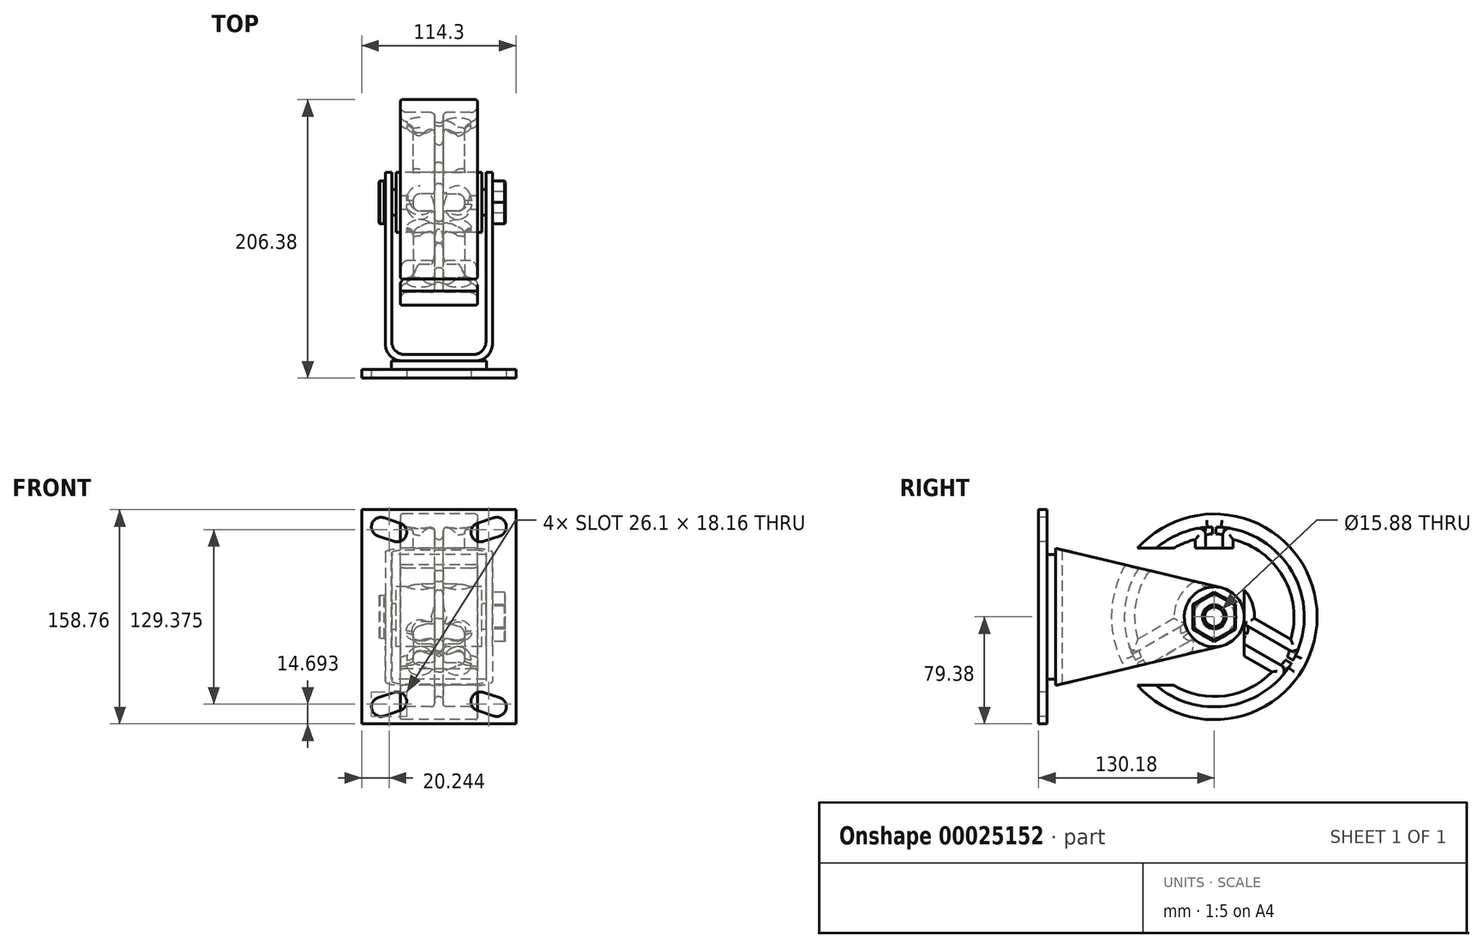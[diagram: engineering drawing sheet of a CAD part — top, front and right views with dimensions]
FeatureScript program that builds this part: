
annotation { "Feature Type Name" : "Feature", "Feature Type Description" : "" }
export const myFeature = defineFeature(function(context is Context, id is Id, definition is map)
    precondition{}
    {
        {
            var Q0;
            Q0=qCreatedBy(makeId("Right.planeOp"),FACE);
            var sketch = newSketch(context, id + "F0", { "sketchPlane" : qUnion([Q0])});
            skCircle(sketch, "E0", {"center": v(0, 0) * mm, "radius": 76.2 * mm});
            skCircle(sketch, "E1", {"center": v(0, 0) * mm, "radius": 9.53 * mm});
            skCircle(sketch, "E2.0", {"center": v(0, 0) * mm, "radius": 66.67 * mm});
            skCircle(sketch, "E3.0", {"center": v(0, 0) * mm, "radius": 22.23 * mm});
            skSolve(sketch);
        }
        {
            var Q0;
            Q0=qSketchRegion(id+"F0",true);
            extrude(context, id + "F1", {"entities" : qUnion([Q0]), "endBound" : BoundingType.SYMMETRIC, "depth" : 57.15 * mm});
        }
        {
            var Q0;
            Q0=makeQuery(id+"F0.imprint","IMPRINT",FACE,{"disambiguationData":[TD([[makeQuery(id+"F0.imprint","IMPRINT",EDGE,{"derivedFrom":sQuery(id+"F0.wireOp",EDGE,"E2.0")}),1.0]])]});
            var Q1;
            Q1=makeQuery(id+"F0.imprint","IMPRINT",FACE,{"disambiguationData":[TD([[makeQuery(id+"F0.imprint","IMPRINT",EDGE,{"derivedFrom":sQuery(id+"F0.wireOp",EDGE,"E1")}),-1.0]])]});
            extrude(context, id + "F2", {"entities" : qUnion([Q0, Q1]), "operationType" : NewBodyOperationType.ADD, "endBound" : BoundingType.SYMMETRIC, "depth" : 6.35 * mm});
        }
        {
            var Q0;
            Q0=qCreatedBy(makeId("Right.planeOp"),FACE);
            var sketch = newSketch(context, id + "F3", { "sketchPlane" : qUnion([Q0])});
            skCircle(sketch, "E4.0", {"center": v(0, 0) * mm, "radius": 22.23 * mm});
            skCircle(sketch, "E5.0", {"center": v(0, 0) * mm, "radius": 9.53 * mm});
            skSolve(sketch);
        }
        {
            var Q0;
            Q0=qSketchRegion(id+"F3",true);
            extrude(context, id + "F4", {"entities" : qUnion([Q0]), "operationType" : NewBodyOperationType.ADD, "endBound" : BoundingType.SYMMETRIC, "depth" : 63.5 * mm});
        }
        {
            var Q0;
            Q0=qCreatedBy(makeId("Right.planeOp"),FACE);
            var sketch = newSketch(context, id + "F5", { "sketchPlane" : qUnion([Q0])});
            skArc(sketch, "E6.0", {"start": v(-60.65, -27.69) * mm, "mid": v(-57.74, -33.34) * mm, "end": v(-54.3, -38.69) * mm});
            skArc(sketch, "E7.0", {"start": v(15.27, -16.15) * mm, "mid": v(19.25, -11.11) * mm, "end": v(21.62, -5.15) * mm});
            skLineSegment(sketch, "E8", {"start": v(0, 0) * mm, "end": v(0, 89.96) * mm, "construction": true});
            skLineSegment(sketch, "E9.0", {"start": v(-6.35, 21.3) * mm, "end": v(-6.35, 66.37) * mm});
            skLineSegment(sketch, "E10.0.MirrorCS", {"start": v(6.35, 21.3) * mm, "end": v(6.35, 66.37) * mm});
            skLineSegment(sketch, "E11.1.0", {"start": v(-15.27, -16.15) * mm, "end": v(-54.3, -38.69) * mm});
            skLineSegment(sketch, "E11.1.1", {"start": v(-21.62, -5.15) * mm, "end": v(-60.65, -27.69) * mm});
            skLineSegment(sketch, "E11.2.0", {"start": v(21.62, -5.15) * mm, "end": v(60.65, -27.69) * mm});
            skLineSegment(sketch, "E11.2.1", {"start": v(15.27, -16.15) * mm, "end": v(54.3, -38.69) * mm});
            skArc(sketch, "E12.trimOffspring", {"start": v(6.35, 66.37) * mm, "mid": v(0, 66.67) * mm, "end": v(-6.35, 66.37) * mm});
            skArc(sketch, "E13.trimOffspring", {"start": v(54.3, -38.69) * mm, "mid": v(57.74, -33.34) * mm, "end": v(60.65, -27.69) * mm});
            skArc(sketch, "E14.trimOffspring", {"start": v(-21.62, -5.15) * mm, "mid": v(-19.25, -11.11) * mm, "end": v(-15.27, -16.15) * mm});
            skArc(sketch, "E15.trimOffspring", {"start": v(6.35, 21.3) * mm, "mid": v(0, 22.22) * mm, "end": v(-6.35, 21.3) * mm});
            skSolve(sketch);
        }
        {
            var Q0;
            Q0=qSketchRegion(id+"F5",true);
            extrude(context, id + "F6", {"entities" : qUnion([Q0]), "operationType" : NewBodyOperationType.ADD, "endBound" : BoundingType.SYMMETRIC, "depth" : 38.1 * mm});
        }
        {
            var Q0;
            {var subQ0=sQuery(id+"F0.wireOp",EDGE,"E2.0");Q0=makeQuery(id+"F6.boolean.opBoolean","SPLIT",FACE,{"disambiguationData":[TD([makeQuery(id+"F6.opExtrude","SWEPT_FACE",FACE,{"disambiguationData":[OSD([sQuery(id+"F5.wireOp",EDGE,"E11.1.0")])]})])],"derivedFrom":makeQuery(id+"F2.opExtrude","CAP_FACE",FACE,{"disambiguationData":[OSD([sQuery(id+"F0.wireOp",EDGE,"E1"),subQ0])],"isStart":false})});}
            var sketch = newSketch(context, id + "F7", { "sketchPlane" : qUnion([Q0])});
            skArc(sketch, "E16.0", {"start": v(-15.86, -25.29) * mm, "mid": v(0, -29.85) * mm, "end": v(15.86, -25.29) * mm});
            skLineSegment(sketch, "E17.0", {"start": v(-15.86, -25.29) * mm, "end": v(-42.7, -40.79) * mm});
            skArc(sketch, "E18.0", {"start": v(-42.7, -40.79) * mm, "mid": v(0, -59.05) * mm, "end": v(42.7, -40.79) * mm});
            skLineSegment(sketch, "E19.0", {"start": v(15.86, -25.29) * mm, "end": v(42.7, -40.79) * mm});
            skArc(sketch, "E20.1.0", {"start": v(29.83, -1.09) * mm, "mid": v(25.85, 14.92) * mm, "end": v(13.97, 26.37) * mm});
            skLineSegment(sketch, "E20.1.1", {"start": v(13.97, 26.37) * mm, "end": v(13.97, 57.38) * mm});
            skArc(sketch, "E20.1.2", {"start": v(56.68, -16.6) * mm, "mid": v(51.14, 29.53) * mm, "end": v(13.97, 57.38) * mm});
            skLineSegment(sketch, "E20.1.3", {"start": v(29.83, -1.09) * mm, "end": v(56.68, -16.6) * mm});
            skArc(sketch, "E20.2.0", {"start": v(-13.97, 26.37) * mm, "mid": v(-25.85, 14.92) * mm, "end": v(-29.83, -1.09) * mm});
            skLineSegment(sketch, "E20.2.1", {"start": v(-29.83, -1.09) * mm, "end": v(-56.68, -16.6) * mm});
            skArc(sketch, "E20.2.2", {"start": v(-13.97, 57.38) * mm, "mid": v(-51.14, 29.53) * mm, "end": v(-56.68, -16.6) * mm});
            skLineSegment(sketch, "E20.2.3", {"start": v(-13.97, 26.37) * mm, "end": v(-13.97, 57.38) * mm});
            skSolve(sketch);
        }
        {
            var Q0;
            Q0=qSketchRegion(id+"F7",true);
            extrude(context, id + "F8", {"entities" : qUnion([Q0]), "operationType" : NewBodyOperationType.REMOVE, "endBound" : BoundingType.THROUGH_ALL, "oppositeDirection" : true, "depth" : 25.4 * mm});
        }
        {
            var Q0;
            {var subQ0=sQuery(id+"F0.wireOp",EDGE,"E2.0");Q0=makeQuery(id+"F6.boolean.opBoolean","SPLIT",FACE,{"disambiguationData":[TD([makeQuery(id+"F6.opExtrude","SWEPT_FACE",FACE,{"disambiguationData":[OSD([sQuery(id+"F5.wireOp",EDGE,"E10.0.MirrorCS")])]})])],"derivedFrom":makeQuery(id+"F2.opExtrude","CAP_FACE",FACE,{"disambiguationData":[OSD([sQuery(id+"F0.wireOp",EDGE,"E1"),subQ0])],"isStart":false})});}
            var Q1;
            {var subQ0=sQuery(id+"F0.wireOp",EDGE,"E2.0");Q1=makeQuery(id+"F6.boolean.opBoolean","SPLIT",FACE,{"disambiguationData":[TD([makeQuery(id+"F6.opExtrude","SWEPT_FACE",FACE,{"disambiguationData":[OSD([sQuery(id+"F5.wireOp",EDGE,"E9.0")])]})])],"derivedFrom":makeQuery(id+"F2.opExtrude","CAP_FACE",FACE,{"disambiguationData":[OSD([sQuery(id+"F0.wireOp",EDGE,"E1"),subQ0])],"isStart":false})});}
            var Q2;
            {var subQ0=sQuery(id+"F0.wireOp",EDGE,"E2.0");Q2=makeQuery(id+"F6.boolean.opBoolean","SPLIT",FACE,{"disambiguationData":[TD([makeQuery(id+"F6.opExtrude","SWEPT_FACE",FACE,{"disambiguationData":[OSD([sQuery(id+"F5.wireOp",EDGE,"E11.1.0")])]})])],"derivedFrom":makeQuery(id+"F2.opExtrude","CAP_FACE",FACE,{"disambiguationData":[OSD([sQuery(id+"F0.wireOp",EDGE,"E1"),subQ0])],"isStart":false})});}
            var Q3;
            {var subQ0=sQuery(id+"F0.wireOp",EDGE,"E2.0");Q3=makeQuery(id+"F6.boolean.opBoolean","SPLIT",FACE,{"disambiguationData":[TD([makeQuery(id+"F6.opExtrude","SWEPT_FACE",FACE,{"disambiguationData":[OSD([sQuery(id+"F5.wireOp",EDGE,"E11.1.0")])]})])],"derivedFrom":makeQuery(id+"F2.opExtrude","CAP_FACE",FACE,{"disambiguationData":[OSD([sQuery(id+"F0.wireOp",EDGE,"E1"),subQ0])],"isStart":true})});}
            var Q4;
            {var subQ0=sQuery(id+"F0.wireOp",EDGE,"E2.0");Q4=makeQuery(id+"F6.boolean.opBoolean","SPLIT",FACE,{"disambiguationData":[TD([makeQuery(id+"F6.opExtrude","SWEPT_FACE",FACE,{"disambiguationData":[OSD([sQuery(id+"F5.wireOp",EDGE,"E10.0.MirrorCS")])]})])],"derivedFrom":makeQuery(id+"F2.opExtrude","CAP_FACE",FACE,{"disambiguationData":[OSD([sQuery(id+"F0.wireOp",EDGE,"E1"),subQ0])],"isStart":true})});}
            var Q5;
            {var subQ0=sQuery(id+"F0.wireOp",EDGE,"E2.0");Q5=makeQuery(id+"F6.boolean.opBoolean","SPLIT",FACE,{"disambiguationData":[TD([makeQuery(id+"F6.opExtrude","SWEPT_FACE",FACE,{"disambiguationData":[OSD([sQuery(id+"F5.wireOp",EDGE,"E9.0")])]})])],"derivedFrom":makeQuery(id+"F2.opExtrude","CAP_FACE",FACE,{"disambiguationData":[OSD([sQuery(id+"F0.wireOp",EDGE,"E1"),subQ0])],"isStart":true})});}
            fillet(context, id + "F9", {"entities" : qUnion([Q0, Q1, Q2, Q3, Q4, Q5]), "radius" : 2.54 * mm, "tangentPropagation" : true, "allowEdgeOverflow" : false});
        }
        {
            var Q0;
            Q0=makeQuery(id+"F6.opExtrude","CAP_FACE",FACE,{"disambiguationData":[OSD([sQuery(id+"F5.wireOp",EDGE,"E9.0"),sQuery(id+"F5.wireOp",EDGE,"E10.0.MirrorCS"),sQuery(id+"F5.wireOp",EDGE,"E12.trimOffspring"),sQuery(id+"F5.wireOp",EDGE,"E15.trimOffspring")])],"isStart":true});
            var Q1;
            {var subQ0=sQuery(id+"F5.wireOp",EDGE,"E10.0.MirrorCS");var subQ1=sQuery(id+"F0.wireOp",EDGE,"E2.0");Q1=makeQuery(id+"F6.boolean.opBoolean","SPLIT",FACE,{"disambiguationData":[TD([makeQuery(id+"F2.opExtrude","CAP_FACE",FACE,{"disambiguationData":[OSD([sQuery(id+"F0.wireOp",EDGE,"E1"),subQ1])],"isStart":true})])],"derivedFrom":makeQuery(id+"F6.opExtrude","SWEPT_FACE",FACE,{"disambiguationData":[OSD([subQ0])]})});}
            var Q2;
            {var subQ0=sQuery(id+"F5.wireOp",EDGE,"E11.2.0");var subQ1=sQuery(id+"F0.wireOp",EDGE,"E2.0");Q2=makeQuery(id+"F6.boolean.opBoolean","SPLIT",FACE,{"disambiguationData":[TD([makeQuery(id+"F2.opExtrude","CAP_FACE",FACE,{"disambiguationData":[OSD([sQuery(id+"F0.wireOp",EDGE,"E1"),subQ1])],"isStart":true})])],"derivedFrom":makeQuery(id+"F6.opExtrude","SWEPT_FACE",FACE,{"disambiguationData":[OSD([subQ0])]})});}
            var Q3;
            Q3=makeQuery(id+"F6.opExtrude","CAP_FACE",FACE,{"disambiguationData":[OSD([sQuery(id+"F5.wireOp",EDGE,"E7.0"),sQuery(id+"F5.wireOp",EDGE,"E11.2.0"),sQuery(id+"F5.wireOp",EDGE,"E11.2.1"),sQuery(id+"F5.wireOp",EDGE,"E13.trimOffspring")])],"isStart":true});
            var Q4;
            Q4=makeQuery(id+"F6.opExtrude","CAP_FACE",FACE,{"disambiguationData":[OSD([sQuery(id+"F5.wireOp",EDGE,"E6.0"),sQuery(id+"F5.wireOp",EDGE,"E11.1.0"),sQuery(id+"F5.wireOp",EDGE,"E11.1.1"),sQuery(id+"F5.wireOp",EDGE,"E14.trimOffspring")])],"isStart":true});
            var Q5;
            Q5=makeQuery(id+"F6.opExtrude","CAP_FACE",FACE,{"disambiguationData":[OSD([sQuery(id+"F5.wireOp",EDGE,"E9.0"),sQuery(id+"F5.wireOp",EDGE,"E10.0.MirrorCS"),sQuery(id+"F5.wireOp",EDGE,"E12.trimOffspring"),sQuery(id+"F5.wireOp",EDGE,"E15.trimOffspring")])],"isStart":false});
            var Q6;
            Q6=makeQuery(id+"F6.opExtrude","CAP_FACE",FACE,{"disambiguationData":[OSD([sQuery(id+"F5.wireOp",EDGE,"E6.0"),sQuery(id+"F5.wireOp",EDGE,"E11.1.0"),sQuery(id+"F5.wireOp",EDGE,"E11.1.1"),sQuery(id+"F5.wireOp",EDGE,"E14.trimOffspring")])],"isStart":false});
            var Q7;
            Q7=makeQuery(id+"F6.opExtrude","CAP_FACE",FACE,{"disambiguationData":[OSD([sQuery(id+"F5.wireOp",EDGE,"E7.0"),sQuery(id+"F5.wireOp",EDGE,"E11.2.0"),sQuery(id+"F5.wireOp",EDGE,"E11.2.1"),sQuery(id+"F5.wireOp",EDGE,"E13.trimOffspring")])],"isStart":false});
            fillet(context, id + "F10", {"entities" : qUnion([Q0, Q1, Q2, Q3, Q4, Q5, Q6, Q7]), "radius" : 5.08 * mm, "tangentPropagation" : true, "allowEdgeOverflow" : false});
        }
        {
            var Q0;
            Q0=makeQuery(id+"F1.opExtrude","CAP_EDGE",EDGE,{"disambiguationData":[OSD([sQuery(id+"F0.wireOp",EDGE,"E2.0")])],"isStart":false});
            var Q1;
            Q1=makeQuery(id+"F1.opExtrude","CAP_EDGE",EDGE,{"disambiguationData":[OSD([sQuery(id+"F0.wireOp",EDGE,"E2.0")])],"isStart":true});
            fillet(context, id + "F11", {"entities" : qUnion([Q0, Q1]), "radius" : 5.08 * mm, "tangentPropagation" : true, "allowEdgeOverflow" : false});
        }
        {
            var Q0;
            Q0=makeQuery(id+"F1.opExtrude","SWEPT_FACE",FACE,{"disambiguationData":[OSD([sQuery(id+"F0.wireOp",EDGE,"E0")])]});
            fillet(context, id + "F12", {"entities" : qUnion([Q0]), "radius" : 1.52 * mm, "tangentPropagation" : true, "allowEdgeOverflow" : false});
        }
        {
            var Q0;
            Q0=qCreatedBy(makeId("Front.planeOp"),FACE);
            cPlane(context, id + "F13", {"entities" : qUnion([Q0]), "cplaneType" : CPlaneType.OFFSET, "offset" : 130.17 * mm, "width" : 152.4 * mm, "height" : 152.4 * mm});
        }
        {
            var Q0;
            Q0=qCreatedBy(id+"F13.planeOp",FACE);
            var sketch = newSketch(context, id + "F14", { "sketchPlane" : qUnion([Q0])});
            skLineSegment(sketch, "E21.rect.bottom", {"start": v(57.15, 79.38) * mm, "end": v(-57.15, 79.38) * mm});
            skLineSegment(sketch, "E21.rect.top", {"start": v(57.15, -79.38) * mm, "end": v(-57.15, -79.38) * mm});
            skLineSegment(sketch, "E21.rect.left", {"start": v(57.15, 79.38) * mm, "end": v(57.15, -79.38) * mm});
            skLineSegment(sketch, "E21.rect.right", {"start": v(-57.15, 79.38) * mm, "end": v(-57.15, -79.38) * mm});
            skPoint(sketch, "E21.rect.middle", {"position": v(0, 0) * mm});
            skLineSegment(sketch, "E22", {"start": v(57.15, 0) * mm, "end": v(-57.15, 0) * mm, "construction": true});
            skLineSegment(sketch, "E23", {"start": v(0, 79.38) * mm, "end": v(0, -79.38) * mm, "construction": true});
            skLineSegment(sketch, "E24.0", {"start": v(57.15, 66.68) * mm, "end": v(-57.15, 66.67) * mm, "construction": true});
            skLineSegment(sketch, "E25.0", {"start": v(57.15, 62.7) * mm, "end": v(-57.15, 62.7) * mm, "construction": true});
            skLineSegment(sketch, "E26.0", {"start": v(42.86, 76.2) * mm, "end": v(42.86, -76.2) * mm, "construction": true});
            skLineSegment(sketch, "E27.0", {"start": v(30.95, 76.2) * mm, "end": v(30.95, -76.2) * mm, "construction": true});
            skArc(sketch, "E28", {"start": v(28.7, 69.45) * mm, "mid": v(24.2, 60.45) * mm, "end": v(33.2, 55.95) * mm});
            skLineSegment(sketch, "E29", {"start": v(45.11, 59.93) * mm, "end": v(33.2, 55.95) * mm});
            skLineSegment(sketch, "E30", {"start": v(28.7, 69.45) * mm, "end": v(40.61, 73.42) * mm});
            skArc(sketch, "E31.trimOffspring", {"start": v(45.11, 59.93) * mm, "mid": v(49.6, 68.93) * mm, "end": v(40.61, 73.42) * mm});
            skArc(sketch, "E32.0.MirrorCS", {"start": v(45.11, -59.93) * mm, "mid": v(49.6, -68.93) * mm, "end": v(40.61, -73.42) * mm});
            skLineSegment(sketch, "E33.0.MirrorCS", {"start": v(28.7, -69.45) * mm, "end": v(40.61, -73.42) * mm});
            skLineSegment(sketch, "E34.0.MirrorCS", {"start": v(45.11, -59.93) * mm, "end": v(33.2, -55.95) * mm});
            skArc(sketch, "E35.0.MirrorCS", {"start": v(28.7, -69.45) * mm, "mid": v(24.2, -60.45) * mm, "end": v(33.2, -55.95) * mm});
            skLineSegment(sketch, "E36.0.MirrorCS", {"start": v(-45.11, -59.93) * mm, "end": v(-33.2, -55.95) * mm});
            skLineSegment(sketch, "E36.1.MirrorCS", {"start": v(-28.7, -69.45) * mm, "end": v(-40.61, -73.42) * mm});
            skLineSegment(sketch, "E36.2.MirrorCS", {"start": v(-42.86, 76.2) * mm, "end": v(-42.86, -76.2) * mm, "construction": true});
            skArc(sketch, "E36.3.MirrorCS", {"start": v(-28.7, 69.45) * mm, "mid": v(-24.2, 60.45) * mm, "end": v(-33.2, 55.95) * mm});
            skArc(sketch, "E36.4.MirrorCS", {"start": v(-45.11, -59.93) * mm, "mid": v(-49.6, -68.93) * mm, "end": v(-40.61, -73.42) * mm});
            skLineSegment(sketch, "E36.5.MirrorCS", {"start": v(-28.7, 69.45) * mm, "end": v(-40.61, 73.42) * mm});
            skArc(sketch, "E36.6.MirrorCS", {"start": v(-45.11, 59.93) * mm, "mid": v(-49.6, 68.93) * mm, "end": v(-40.61, 73.42) * mm});
            skLineSegment(sketch, "E36.7.MirrorCS", {"start": v(-30.95, 76.2) * mm, "end": v(-30.95, -76.2) * mm, "construction": true});
            skLineSegment(sketch, "E36.8.MirrorCS", {"start": v(-45.11, 59.93) * mm, "end": v(-33.2, 55.95) * mm});
            skArc(sketch, "E36.9.MirrorCS", {"start": v(-28.7, -69.45) * mm, "mid": v(-24.2, -60.45) * mm, "end": v(-33.2, -55.95) * mm});
            skSolve(sketch);
        }
        {
            var Q0;
            Q0=makeQuery(id+"F14.imprint","IMPRINT",FACE,{"disambiguationData":[TD([[makeQuery(id+"F14.imprint","IMPRINT",EDGE,{"derivedFrom":sQuery(id+"F14.wireOp",EDGE,"E21.rect.bottom")}),1.0]])]});
            extrude(context, id + "F15", {"entities" : qUnion([Q0]), "oppositeDirection" : true, "depth" : 6.38 * mm});
        }
        {
            var Q0;
            Q0=qCreatedBy(makeId("Top.planeOp"),FACE);
            var sketch = newSketch(context, id + "F16", { "sketchPlane" : qUnion([Q0])});
            skLineSegment(sketch, "E37.0", {"start": v(-34.92, 22.23) * mm, "end": v(-34.92, -112.67) * mm});
            skLineSegment(sketch, "E38.0", {"start": v(0, -117.45) * mm, "end": v(-39.7, -117.45) * mm});
            skLineSegment(sketch, "E39.0", {"start": v(0, -112.67) * mm, "end": v(-34.92, -112.67) * mm});
            skLineSegment(sketch, "E40.0", {"start": v(-39.7, 22.23) * mm, "end": v(-39.7, -117.45) * mm});
            skLineSegment(sketch, "E41", {"start": v(0, 0) * mm, "end": v(0, -149.02) * mm, "construction": true});
            skLineSegment(sketch, "E42", {"start": v(-39.7, 22.23) * mm, "end": v(-34.92, 22.23) * mm});
            skLineSegment(sketch, "E43.0.MirrorCS", {"start": v(0, -112.67) * mm, "end": v(34.92, -112.67) * mm});
            skLineSegment(sketch, "E44.0.MirrorCS", {"start": v(0, -117.45) * mm, "end": v(39.7, -117.45) * mm});
            skLineSegment(sketch, "E45.0.MirrorCS", {"start": v(34.92, 22.23) * mm, "end": v(34.92, -112.67) * mm});
            skLineSegment(sketch, "E46.0.MirrorCS", {"start": v(39.7, 22.23) * mm, "end": v(39.7, -117.45) * mm});
            skLineSegment(sketch, "E47.0.MirrorCS", {"start": v(39.7, 22.23) * mm, "end": v(34.92, 22.23) * mm});
            skSolve(sketch);
        }
        {
            var Q0;
            Q0=qSketchRegion(id+"F16",true);
            extrude(context, id + "F17", {"entities" : qUnion([Q0]), "endBound" : BoundingType.SYMMETRIC, "depth" : 101.6 * mm});
        }
        {
            var Q0;
            Q0=makeQuery(id+"F17.opExtrude","SWEPT_FACE",FACE,{"disambiguationData":[OSD([sQuery(id+"F16.wireOp",EDGE,"E40.0")])]});
            var sketch = newSketch(context, id + "F18", { "sketchPlane" : qUnion([Q0])});
            skArc(sketch, "E48.0", {"start": v(-5.15, -21.62) * mm, "mid": v(-22.23, 0) * mm, "end": v(-5.15, 21.62) * mm});
            skLineSegment(sketch, "E49", {"start": v(117.45, 50.8) * mm, "end": v(-5.15, 21.62) * mm});
            skLineSegment(sketch, "E50", {"start": v(117.45, -50.8) * mm, "end": v(-5.15, -21.62) * mm});
            skCircle(sketch, "E51.0", {"center": v(0, 0) * mm, "radius": 9.53 * mm});
            skLineSegment(sketch, "E52.0", {"start": v(-22.23, 50.8) * mm, "end": v(117.45, 50.8) * mm});
            skLineSegment(sketch, "E53.0", {"start": v(-22.23, 50.8) * mm, "end": v(-22.23, -50.8) * mm});
            skLineSegment(sketch, "E54.0", {"start": v(-22.23, -50.8) * mm, "end": v(117.45, -50.8) * mm});
            skSolve(sketch);
        }
        {
            var Q0;
            Q0=qSketchRegion(id+"F18",true);
            extrude(context, id + "F19", {"entities" : qUnion([Q0]), "operationType" : NewBodyOperationType.REMOVE, "oppositeDirection" : true, "depth" : 101.6 * mm});
        }
        {
            var Q0;
            Q0=makeQuery(id+"F17.opExtrude","SWEPT_EDGE",EDGE,{"disambiguationData":[OSD([sQuery(id+"F16.wireOp",EDGE,"E43.0.MirrorCS"),sQuery(id+"F16.wireOp",EDGE,"E45.0.MirrorCS")])]});
            var Q1;
            Q1=makeQuery(id+"F17.opExtrude","SWEPT_EDGE",EDGE,{"disambiguationData":[OSD([sQuery(id+"F16.wireOp",EDGE,"E37.0"),sQuery(id+"F16.wireOp",EDGE,"E39.0")])]});
            fillet(context, id + "F20", {"entities" : qUnion([Q0, Q1]), "radius" : 9.52 * mm, "tangentPropagation" : true, "allowEdgeOverflow" : false});
        }
        {
            var Q0;
            Q0=makeQuery(id+"F17.opExtrude","SWEPT_EDGE",EDGE,{"disambiguationData":[OSD([sQuery(id+"F16.wireOp",EDGE,"E44.0.MirrorCS"),sQuery(id+"F16.wireOp",EDGE,"E46.0.MirrorCS")])]});
            var Q1;
            Q1=makeQuery(id+"F17.opExtrude","SWEPT_EDGE",EDGE,{"disambiguationData":[OSD([sQuery(id+"F16.wireOp",EDGE,"E38.0"),sQuery(id+"F16.wireOp",EDGE,"E40.0")])]});
            fillet(context, id + "F21", {"entities" : qUnion([Q0, Q1]), "radius" : 12.7 * mm, "tangentPropagation" : true, "allowEdgeOverflow" : false});
        }
        {
            var Q0;
            Q0=makeQuery(id+"F17.opExtrude","SWEPT_FACE",FACE,{"disambiguationData":[OSD([sQuery(id+"F16.wireOp",EDGE,"E40.0")])]});
            var sketch = newSketch(context, id + "F22", { "sketchPlane" : qUnion([Q0])});
            skCircle(sketch, "E55", {"center": v(0, 0) * mm, "radius": 15.88 * mm});
            skSolve(sketch);
        }
        {
            var Q0;
            Q0=qSketchRegion(id+"F22",true);
            extrude(context, id + "F23", {"entities" : qUnion([Q0]), "depth" : 4.78 * mm});
        }
        {
            var Q0;
            Q0=makeQuery(id+"F23.opExtrude","CAP_FACE",FACE,{"disambiguationData":[OSD([sQuery(id+"F22.wireOp",EDGE,"E55")])],"isStart":true});
            var sketch = newSketch(context, id + "F24", { "sketchPlane" : qUnion([Q0])});
            skCircle(sketch, "E56", {"center": v(0, 0) * mm, "radius": 9.53 * mm});
            skSolve(sketch);
        }
        {
            var Q0;
            Q0=qSketchRegion(id+"F24",true);
            extrude(context, id + "F25", {"entities" : qUnion([Q0]), "operationType" : NewBodyOperationType.ADD, "depth" : 79.43 * mm});
        }
        {
            var Q0;
            Q0=makeQuery(id+"F25.opExtrude","CAP_FACE",FACE,{"disambiguationData":[OSD([sQuery(id+"F24.wireOp",EDGE,"E56")])],"isStart":false});
            var sketch = newSketch(context, id + "F26", { "sketchPlane" : qUnion([Q0])});
            skCircle(sketch, "E57", {"center": v(0, 0) * mm, "radius": 7.94 * mm});
            skSolve(sketch);
        }
        {
            var Q0;
            Q0=qSketchRegion(id+"F26",true);
            extrude(context, id + "F27", {"entities" : qUnion([Q0]), "operationType" : NewBodyOperationType.ADD, "depth" : 9.52 * mm});
        }
        {
            var Q0;
            Q0=makeQuery(id+"F27.opExtrude","CAP_FACE",FACE,{"disambiguationData":[OSD([sQuery(id+"F26.wireOp",EDGE,"E57")])],"isStart":false});
            chamfer(context, id + "F28", {"entities" : qUnion([Q0]), "width" : 0.76 * mm, "tangentPropagation" : true});
        }
        {
            var Q0;
            Q0=makeQuery(id+"F25.opExtrude","CAP_FACE",FACE,{"disambiguationData":[OSD([sQuery(id+"F24.wireOp",EDGE,"E56")])],"isStart":false});
            var sketch = newSketch(context, id + "F29", { "sketchPlane" : qUnion([Q0])});
            skCircle(sketch, "E58.cCircle", {"center": v(0, 0) * mm, "radius": 15.88 * mm, "construction": true});
            skLineSegment(sketch, "E58.0", {"start": v(15.88, 9.17) * mm, "end": v(15.88, -9.17) * mm});
            skLineSegment(sketch, "E58.1", {"start": v(15.88, -9.17) * mm, "end": v(0, -18.33) * mm});
            skLineSegment(sketch, "E58.2", {"start": v(0, -18.33) * mm, "end": v(-15.88, -9.17) * mm});
            skLineSegment(sketch, "E58.3", {"start": v(-15.88, -9.17) * mm, "end": v(-15.88, 9.17) * mm});
            skLineSegment(sketch, "E58.4", {"start": v(-15.88, 9.17) * mm, "end": v(0, 18.33) * mm});
            skLineSegment(sketch, "E58.5", {"start": v(0, 18.33) * mm, "end": v(15.87, 9.17) * mm});
            skPoint(sketch, "E58.0.midPoint", {"position": v(15.88, 0) * mm});
            skCircle(sketch, "E59.0", {"center": v(0, 0) * mm, "radius": 7.94 * mm});
            skSolve(sketch);
        }
        {
            var Q0;
            Q0=qSketchRegion(id+"F29",true);
            var Q1;
            Q1=makeQuery(id+"F27.opExtrude","CAP_FACE",FACE,{"disambiguationData":[OSD([sQuery(id+"F26.wireOp",EDGE,"E57")])],"isStart":false});
            extrude(context, id + "F30", {"entities" : qUnion([Q0]), "endBound" : BoundingType.UP_TO_SURFACE, "endBoundEntityFace" : qUnion([Q1]), "depth" : 25.4 * mm});
        }
        {
            var Q0;
            Q0=makeQuery(id+"F15.opExtrude","CAP_FACE",FACE,{"disambiguationData":[OSD([sQuery(id+"F14.wireOp",EDGE,"E21.rect.bottom"),sQuery(id+"F14.wireOp",EDGE,"E21.rect.top"),sQuery(id+"F14.wireOp",EDGE,"E21.rect.left"),sQuery(id+"F14.wireOp",EDGE,"E21.rect.right"),sQuery(id+"F14.wireOp",EDGE,"E28"),sQuery(id+"F14.wireOp",EDGE,"E29"),sQuery(id+"F14.wireOp",EDGE,"E30"),sQuery(id+"F14.wireOp",EDGE,"E31.trimOffspring"),sQuery(id+"F14.wireOp",EDGE,"E32.0.MirrorCS"),sQuery(id+"F14.wireOp",EDGE,"E33.0.MirrorCS"),sQuery(id+"F14.wireOp",EDGE,"E34.0.MirrorCS"),sQuery(id+"F14.wireOp",EDGE,"E35.0.MirrorCS"),sQuery(id+"F14.wireOp",EDGE,"E36.0.MirrorCS"),sQuery(id+"F14.wireOp",EDGE,"E36.1.MirrorCS"),sQuery(id+"F14.wireOp",EDGE,"E36.3.MirrorCS"),sQuery(id+"F14.wireOp",EDGE,"E36.4.MirrorCS"),sQuery(id+"F14.wireOp",EDGE,"E36.5.MirrorCS"),sQuery(id+"F14.wireOp",EDGE,"E36.6.MirrorCS"),sQuery(id+"F14.wireOp",EDGE,"E36.8.MirrorCS"),sQuery(id+"F14.wireOp",EDGE,"E36.9.MirrorCS")])],"isStart":false});
            var sketch = newSketch(context, id + "F31", { "sketchPlane" : qUnion([Q0])});
            skLineSegment(sketch, "E60.rect.bottom", {"start": v(-35.19, -46.09) * mm, "end": v(35.19, -46.09) * mm});
            skLineSegment(sketch, "E60.rect.top", {"start": v(-35.19, 46.09) * mm, "end": v(35.19, 46.09) * mm});
            skLineSegment(sketch, "E60.rect.left", {"start": v(-35.19, -46.09) * mm, "end": v(-35.19, 46.09) * mm});
            skLineSegment(sketch, "E60.rect.right", {"start": v(35.19, -46.09) * mm, "end": v(35.19, 46.09) * mm});
            skPoint(sketch, "E60.rect.middle", {"position": v(0, 0) * mm});
            skSolve(sketch);
        }
        {
            var Q0;
            Q0=qSketchRegion(id+"F31",true);
            extrude(context, id + "F32", {"entities" : qUnion([Q0]), "depth" : 6.35 * mm});
        }
        {
            var Q0;
            Q0=makeQuery(id+"F30.opExtrude","CAP_FACE",FACE,{"disambiguationData":[OSD([sQuery(id+"F29.wireOp",EDGE,"E58.0"),sQuery(id+"F29.wireOp",EDGE,"E58.1"),sQuery(id+"F29.wireOp",EDGE,"E58.2"),sQuery(id+"F29.wireOp",EDGE,"E58.3"),sQuery(id+"F29.wireOp",EDGE,"E58.4"),sQuery(id+"F29.wireOp",EDGE,"E58.5"),sQuery(id+"F29.wireOp",EDGE,"E59.0")])],"isStart":false});
            chamfer(context, id + "F33", {"entities" : qUnion([Q0]), "width" : 0.76 * mm, "tangentPropagation" : true});
        }
        {
            var Q0;
            Q0=makeQuery(id+"F23.opExtrude","SWEPT_FACE",FACE,{"disambiguationData":[OSD([sQuery(id+"F22.wireOp",EDGE,"E55")])]});
            chamfer(context, id + "F34", {"entities" : qUnion([Q0]), "width" : 0.76 * mm, "tangentPropagation" : true});
        }
    });
